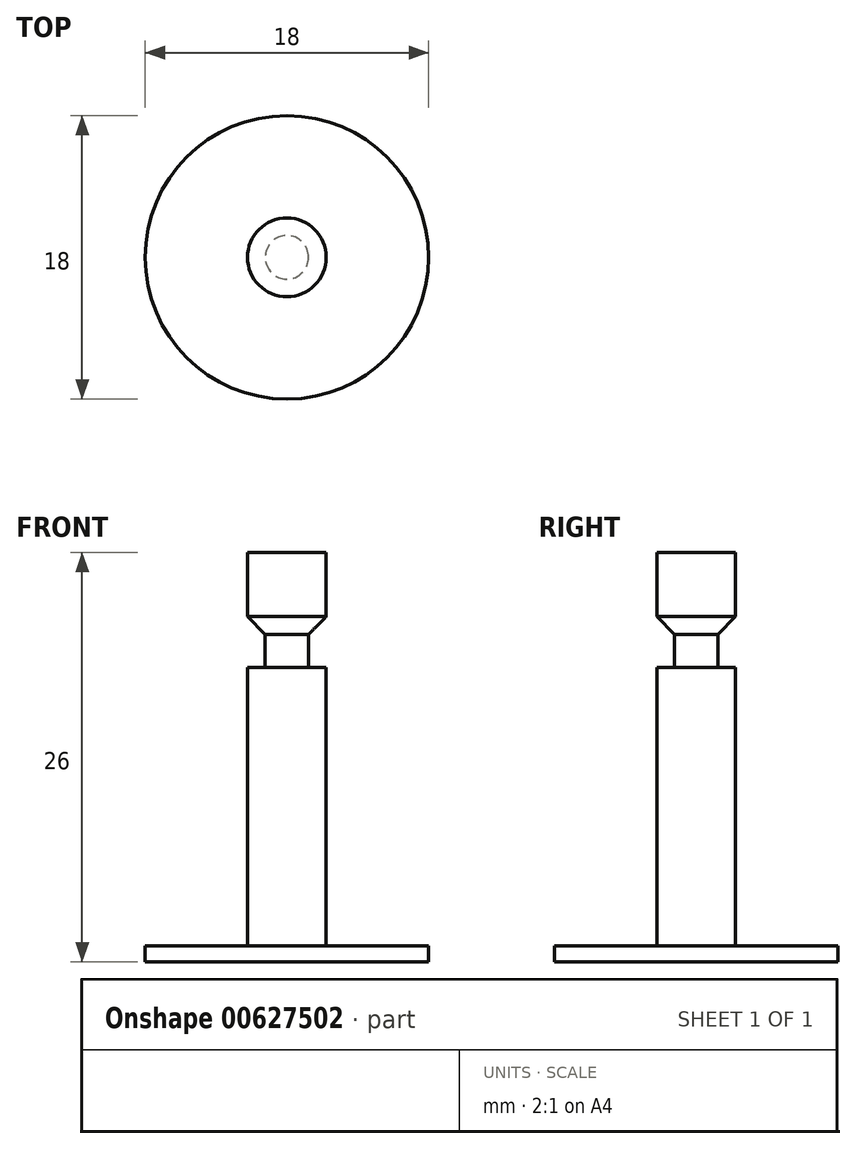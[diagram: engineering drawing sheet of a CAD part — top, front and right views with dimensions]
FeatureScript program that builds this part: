
annotation { "Feature Type Name" : "Feature", "Feature Type Description" : "" }
export const myFeature = defineFeature(function(context is Context, id is Id, definition is map)
    precondition{}
    {
        {
            var Q0;
            Q0=qCreatedBy(makeId("Top.planeOp"),FACE);
            var sketch = newSketch(context, id + "F0", { "sketchPlane" : qUnion([Q0])});
            skCircle(sketch, "E0", {"center": v(0, 0) * mm, "radius": 9 * mm});
            skSolve(sketch);
        }
        {
            var Q0;
            Q0 = qSketchRegion(id + "F0", true);
            extrude(context, id + "F1", {"entities" : qUnion([Q0]), "depth" : 1 * mm, "offsetDistance" : 25 * mm});
        }
        {
            var Q0;
            Q0=makeQuery(id+"F1.opExtrude","CAP_FACE",FACE,{"disambiguationData":[OSD([sQuery(id+"F0.wireOp",EDGE,"E0")])],"isStart":false});
            var sketch = newSketch(context, id + "F2", { "sketchPlane" : qUnion([Q0])});
            skCircle(sketch, "E1", {"center": v(0, 0) * mm, "radius": 2.5 * mm});
            skSolve(sketch);
        }
        {
            var Q0;
            Q0 = qSketchRegion(id + "F2", true);
            extrude(context, id + "F3", {"entities" : qUnion([Q0]), "operationType" : NewBodyOperationType.ADD, "depth" : 25 * mm, "offsetDistance" : 25 * mm});
        }
        {
            var Q0;
            Q0=qCreatedBy(makeId("Right.planeOp"),FACE);
            var sketch = newSketch(context, id + "F4", { "sketchPlane" : qUnion([Q0])});
            skLineSegment(sketch, "E2", {"start": v(0, 0) * mm, "end": v(0, 19.03) * mm, "construction": true});
            skSolve(sketch);
        }
        {
            var Q0;
            Q0=qCreatedBy(makeId("Right.planeOp"),FACE);
            var sketch = newSketch(context, id + "F5", { "sketchPlane" : qUnion([Q0])});
            skLineSegment(sketch, "E3.bottom", {"start": v(-2.54, 18.69) * mm, "end": v(-1.38, 18.69) * mm});
            skLineSegment(sketch, "E3.top", {"start": v(-2.54, 21.97) * mm, "end": v(-1.38, 20.8) * mm});
            skLineSegment(sketch, "E3.left", {"start": v(-2.54, 18.69) * mm, "end": v(-2.54, 21.97) * mm});
            skLineSegment(sketch, "E3.right", {"start": v(-1.38, 18.69) * mm, "end": v(-1.38, 20.8) * mm});
            skSolve(sketch);
        }
        {
            var Q0;
            Q0=makeQuery(id+"F5.imprint","IMPRINT",FACE,{"disambiguationData":[TD([[makeQuery(id+"F5.imprint","IMPRINT",EDGE,{"derivedFrom":sQuery(id+"F5.wireOp",EDGE,"E3.bottom")}),1.0]])]});
            var Q1;
            Q1=sQuery(id+"F4.wireOp",EDGE,"E2");
            revolve(context, id + "F6", {"operationType" : NewBodyOperationType.REMOVE, "entities" : qUnion([Q0]), "axis" : qUnion([Q1]), "revolveType" : RevolveType.FULL, "oppositeDirection" : true});
        }
    });
